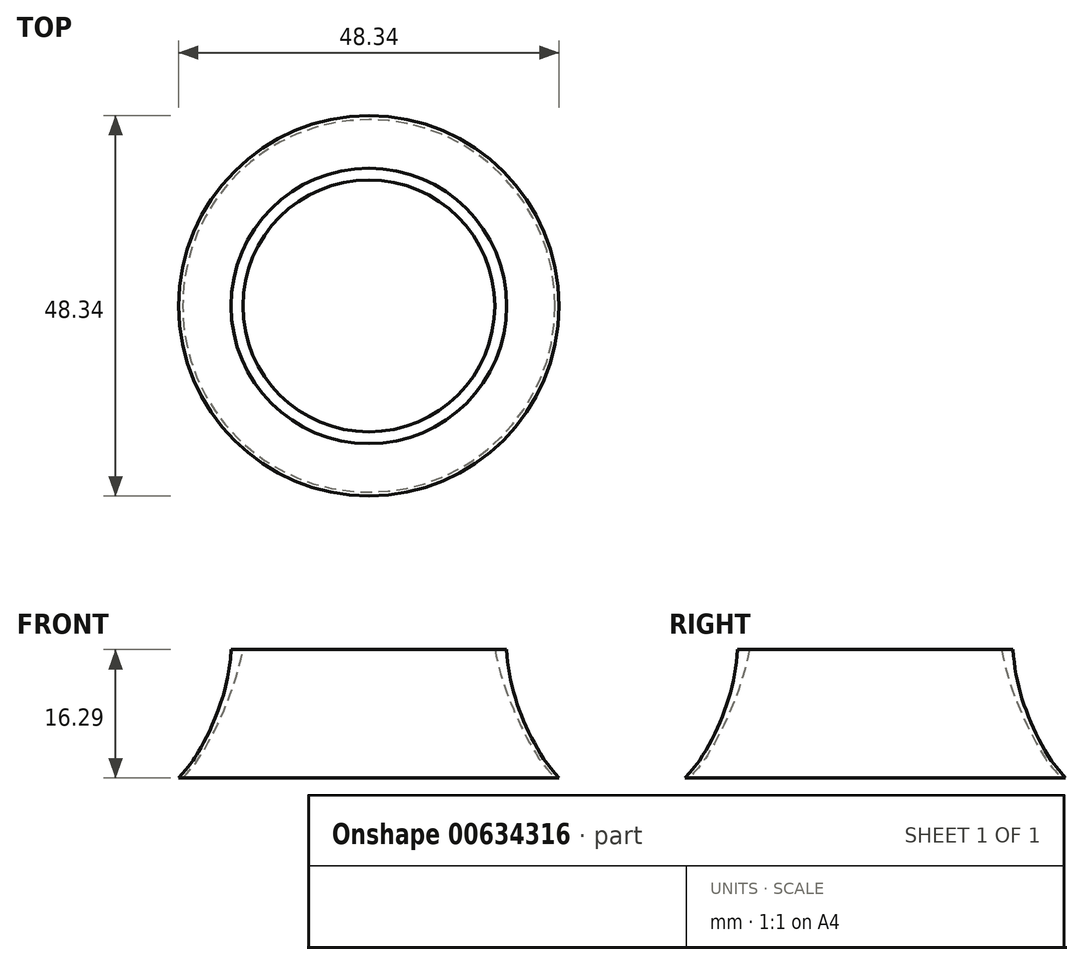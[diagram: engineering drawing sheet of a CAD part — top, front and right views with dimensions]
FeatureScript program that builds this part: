
annotation { "Feature Type Name" : "Feature", "Feature Type Description" : "" }
export const myFeature = defineFeature(function(context is Context, id is Id, definition is map)
    precondition{}
    {
        {
            var Q0;
            Q0=qCreatedBy(makeId("Top.planeOp"),FACE);
            var sketch = newSketch(context, id + "F0", { "sketchPlane" : qUnion([Q0])});
            skCircle(sketch, "E0", {"center": v(0, 0) * mm, "radius": 24.16 * mm});
            skCircle(sketch, "E1", {"center": v(0, 0) * mm, "radius": 23.66 * mm});
            skLineSegment(sketch, "E2", {"start": v(24.16, 0) * mm, "end": v(-24.16, 0) * mm, "construction": true});
            skLineSegment(sketch, "E3", {"start": v(0, 24.16) * mm, "end": v(0, -24.16) * mm, "construction": true});
            skCircle(sketch, "E4", {"center": v(0, 0) * mm, "radius": 14.34 * mm});
            skLineSegment(sketch, "E5", {"start": v(0, 0) * mm, "end": v(-23.66, 0) * mm, "construction": true});
            skSolve(sketch);
        }
        {
            var Q0;
            Q0=qCreatedBy(makeId("Top.planeOp"),FACE);
            cPlane(context, id + "F1", {"entities" : qUnion([Q0]), "cplaneType" : CPlaneType.OFFSET, "offset" : 16.29 * mm, "width" : 152.4 * mm, "height" : 152.4 * mm});
        }
        {
            var Q0;
            Q0=qCreatedBy(id+"F1.planeOp",FACE);
            var sketch = newSketch(context, id + "F2", { "sketchPlane" : qUnion([Q0])});
            skCircle(sketch, "E6", {"center": v(0, 0) * mm, "radius": 17.5 * mm});
            skCircle(sketch, "E7", {"center": v(0, 0) * mm, "radius": 16 * mm});
            skLineSegment(sketch, "E8", {"start": v(17.5, 0) * mm, "end": v(-17.5, 0) * mm, "construction": true});
            skLineSegment(sketch, "E9", {"start": v(0, -17.5) * mm, "end": v(0, 17.5) * mm, "construction": true});
            skLineSegment(sketch, "E10", {"start": v(-17.5, 0) * mm, "end": v(-16, 0) * mm, "construction": true});
            skSolve(sketch);
        }
        {
            var Q0;
            Q0=qCreatedBy(makeId("Front.planeOp"),FACE);
            var sketch = newSketch(context, id + "F3", { "sketchPlane" : qUnion([Q0])});
            skFitSpline(sketch, "E11", {"points": [v(-24.16, 0) * mm, v(-21.98, 2.75) * mm, v(-17.5, 16.29) * mm], "startDerivative": vector(12.68, 15.24) * mm, "endDerivative": vector(1.35, 28) * mm});
            skLineSegment(sketch, "E12", {"start": v(-24.16, 0) * mm, "end": v(-23.66, 0) * mm});
            skFitSpline(sketch, "E13", {"points": [v(-23.66, 0) * mm, v(-21.48, 2.66) * mm, v(-16, 16.29) * mm], "startDerivative": vector(12.6, 13.87) * mm, "endDerivative": vector(5.27, 27.77) * mm});
            skLineSegment(sketch, "E14", {"start": v(-17.5, 16.29) * mm, "end": v(-16, 16.29) * mm});
            skSolve(sketch);
        }
        {
            var Q0;
            Q0=makeQuery(id+"F3.imprint","IMPRINT",FACE,{"disambiguationData":[TD([[makeQuery(id+"F3.imprint","IMPRINT",EDGE,{"derivedFrom":sQuery(id+"F3.wireOp",EDGE,"E11")}),-1.0]])]});
            var Q1;
            Q1=sQuery(id+"F2.wireOp",EDGE,"E6");
            sweep(context, id + "F4", {"profiles" : qUnion([Q0]), "path" : qUnion([Q1])});
        }
    });
